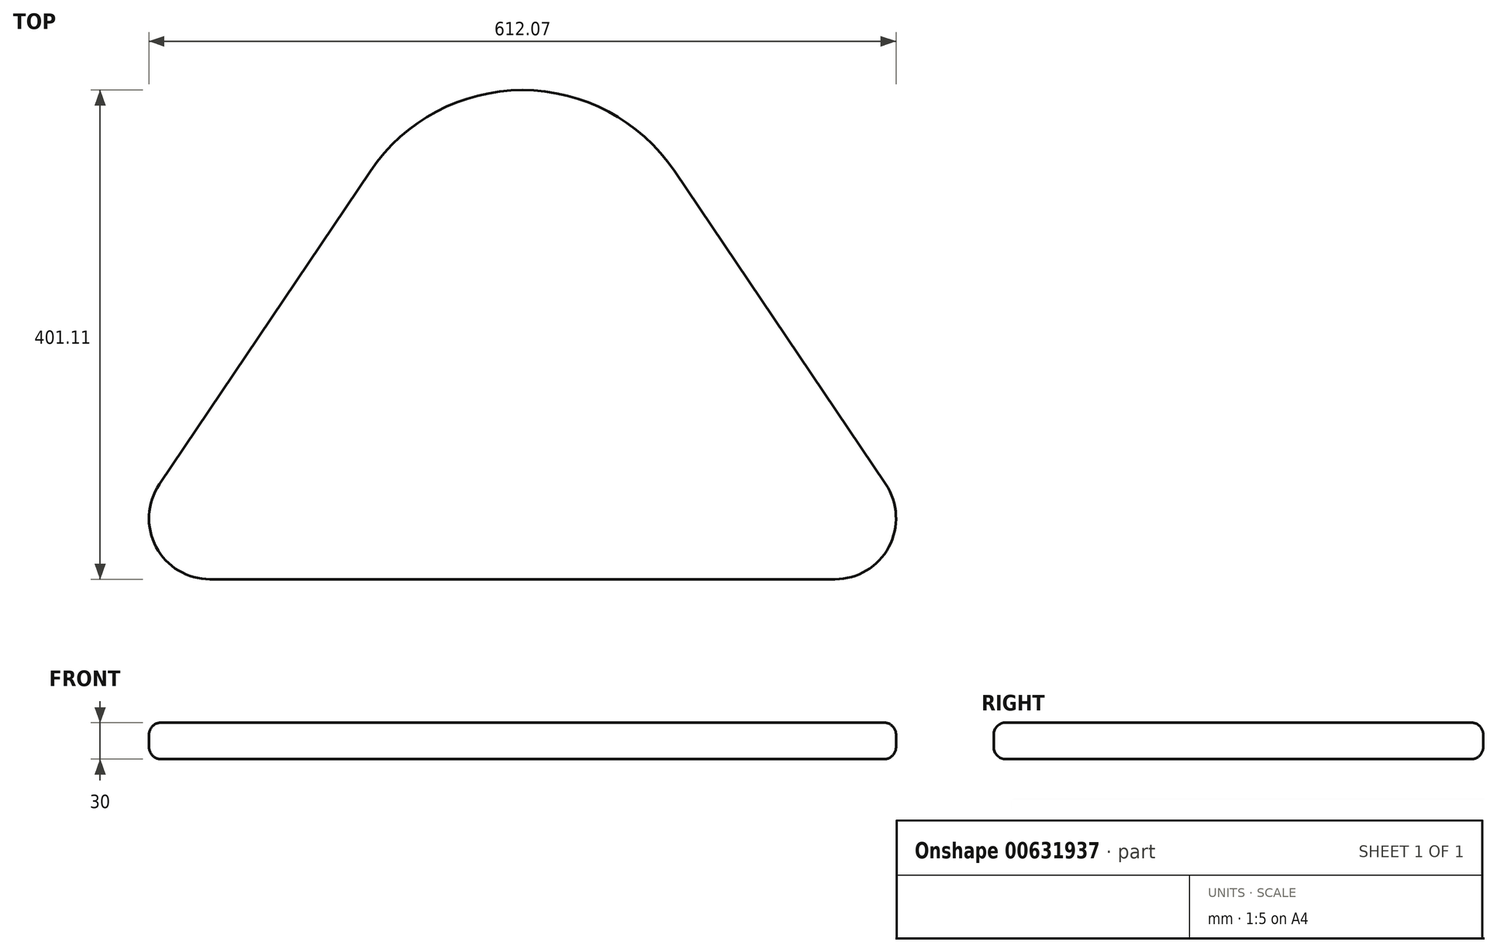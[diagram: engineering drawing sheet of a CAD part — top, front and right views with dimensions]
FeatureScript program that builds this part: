
annotation { "Feature Type Name" : "Feature", "Feature Type Description" : "" }
export const myFeature = defineFeature(function(context is Context, id is Id, definition is map)
    precondition{}
    {
        {
            var Q0;
            Q0=qCreatedBy(makeId("Top.planeOp"),FACE);
            var sketch = newSketch(context, id + "F0", { "sketchPlane" : qUnion([Q0])});
            skLineSegment(sketch, "E0", {"start": v(-256, -74.64) * mm, "end": v(256.07, -74.64) * mm});
            skLineSegment(sketch, "E1", {"start": v(124.42, 260.28) * mm, "end": v(297.54, 3.3) * mm});
            skLineSegment(sketch, "E2", {"start": v(-124.4, 260.26) * mm, "end": v(-297.47, 3.3) * mm});
            skPoint(sketch, "E3.visualSharp", {"position": v(350.05, -74.64) * mm});
            skArc(sketch, "E3.filletArc", {"start": v(256.07, -74.64) * mm, "mid": v(300.21, -48.12) * mm, "end": v(297.54, 3.3) * mm});
            skPoint(sketch, "E4.visualSharp", {"position": v(-349.95, -74.64) * mm});
            skArc(sketch, "E4.filletArc", {"start": v(-297.47, 3.3) * mm, "mid": v(-300.14, -48.13) * mm, "end": v(-256, -74.64) * mm});
            skPoint(sketch, "E5.visualSharp", {"position": v(0, 444.97) * mm});
            skArc(sketch, "E5.filletArc", {"start": v(124.42, 260.28) * mm, "mid": v(0, 326.47) * mm, "end": v(-124.4, 260.26) * mm});
            skSolve(sketch);
        }
        {
            var Q0;
            Q0 = qSketchRegion(id + "F0", true);
            var Q1;
            Q1=makeQuery(id+"F0.imprint","IMPRINT",FACE,{"disambiguationData":[TD([[makeQuery(id+"F0.imprint","IMPRINT",EDGE,{"derivedFrom":sQuery(id+"F0.wireOp",EDGE,"E0")}),1.0]])]});
            extrude(context, id + "F1", {"entities" : qUnion([Q0, Q1]), "depth" : 30 * mm, "offsetDistance" : 25 * mm});
        }
        {
            var Q0;
            Q0=makeQuery(id+"F1.opExtrude","CAP_EDGE",EDGE,{"disambiguationData":[OSD([sQuery(id+"F0.wireOp",EDGE,"E2")])],"isStart":false});
            var Q1;
            Q1=makeQuery(id+"F1.opExtrude","CAP_EDGE",EDGE,{"disambiguationData":[OSD([sQuery(id+"F0.wireOp",EDGE,"E2")])],"isStart":true});
            fillet(context, id + "F2", {"entities" : qUnion([Q0, Q1]), "radius" : 10 * mm, "tangentPropagation" : true, "allowEdgeOverflow" : false});
        }
    });
